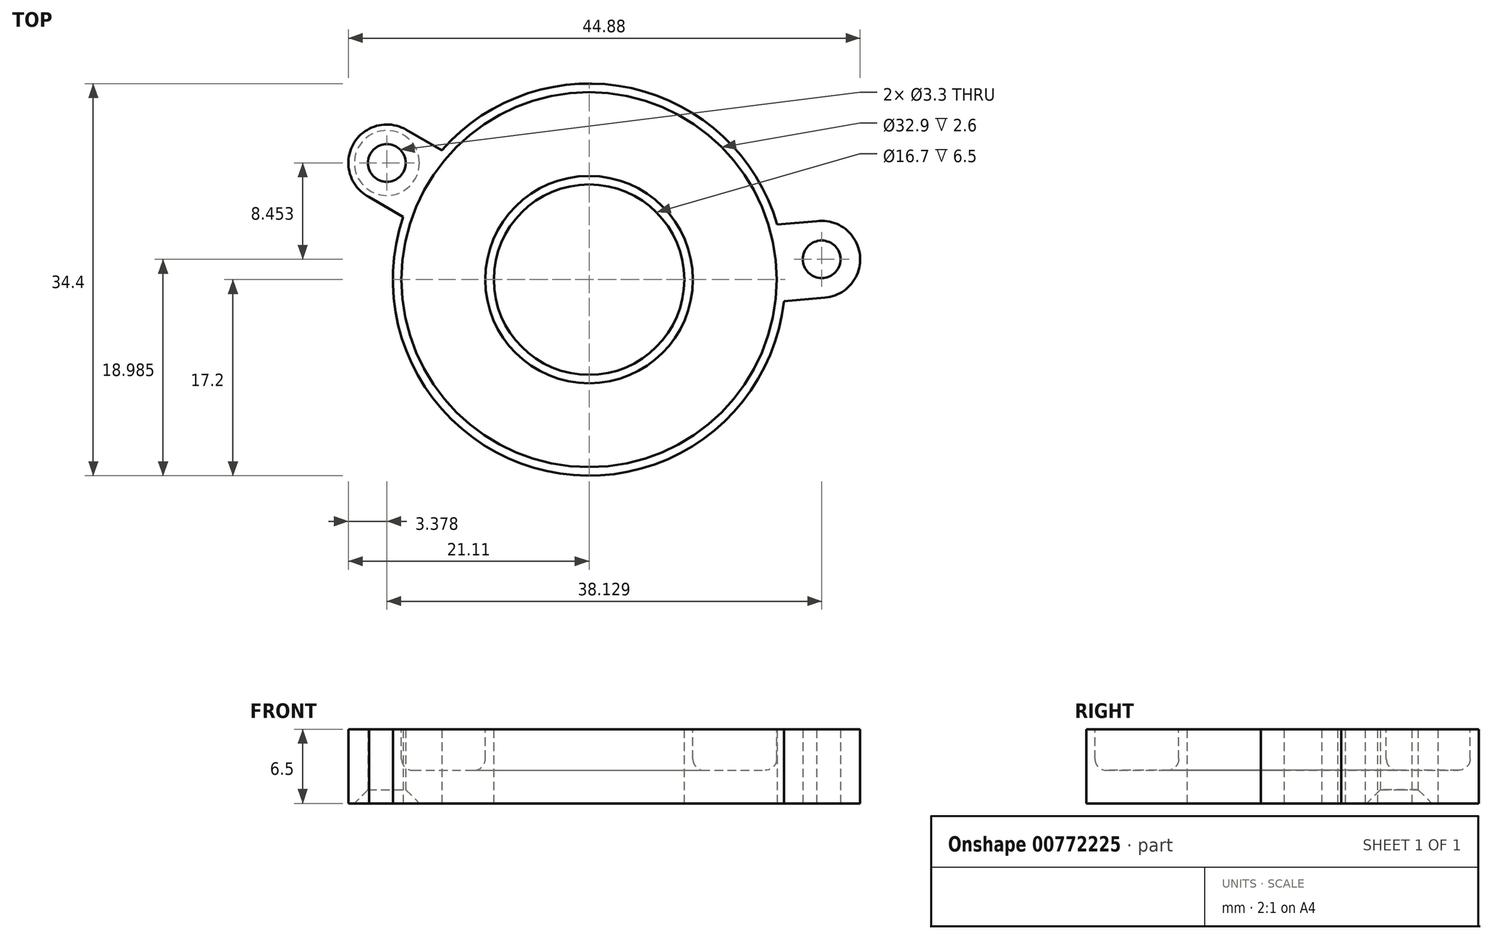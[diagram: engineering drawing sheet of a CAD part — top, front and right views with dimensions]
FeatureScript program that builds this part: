
annotation { "Feature Type Name" : "Feature", "Feature Type Description" : "" }
export const myFeature = defineFeature(function(context is Context, id is Id, definition is map)
    precondition{}
    {
        {
            var Q0;
            Q0=qCreatedBy(makeId("Right.planeOp"),FACE);
            var sketch = newSketch(context, id + "F0", { "sketchPlane" : qUnion([Q0])});
            skLineSegment(sketch, "E0.bottom", {"start": v(17.2, 0) * mm, "end": v(8.35, 0) * mm});
            skLineSegment(sketch, "E0.top", {"start": v(17.2, 6.5) * mm, "end": v(16.45, 6.5) * mm});
            skLineSegment(sketch, "E0.left", {"start": v(17.2, 6.5) * mm, "end": v(17.2, 0) * mm});
            skLineSegment(sketch, "E0.right", {"start": v(8.35, 6.5) * mm, "end": v(8.35, 0) * mm});
            skLineSegment(sketch, "E1.top", {"start": v(16.45, 2.9) * mm, "end": v(9.1, 2.9) * mm});
            skLineSegment(sketch, "E1.left", {"start": v(16.45, 2.9) * mm, "end": v(16.45, 6.5) * mm});
            skLineSegment(sketch, "E1.right", {"start": v(9.1, 2.9) * mm, "end": v(9.1, 6.5) * mm});
            skLineSegment(sketch, "E2.trimOffspring", {"start": v(9.1, 6.5) * mm, "end": v(8.35, 6.5) * mm});
            skLineSegment(sketch, "E3", {"start": v(0, 14.54) * mm, "end": v(0, -19.43) * mm, "construction": true});
            skSolve(sketch);
        }
        {
            var Q0;
            Q0=qSketchRegion(id+"F0",true);
            var Q1;
            Q1=sQuery(id+"F0.wireOp",EDGE,"E3");
            revolve(context, id + "F1", {"entities" : qUnion([Q0]), "axis" : qUnion([Q1]), "revolveType" : RevolveType.FULL});
        }
        {
            var Q0;
            Q0=qCreatedBy(makeId("Top.planeOp"),FACE);
            var sketch = newSketch(context, id + "F2", { "sketchPlane" : qUnion([Q0])});
            skArc(sketch, "E4", {"start": v(-16.04, 13.16) * mm, "mid": v(-20.69, 11.86) * mm, "end": v(-19.3, 7.25) * mm});
            skLineSegment(sketch, "E5", {"start": v(0, 0) * mm, "end": v(-17.73, 10.24) * mm, "construction": true});
            skLineSegment(sketch, "E6", {"start": v(-19.3, 7.25) * mm, "end": v(-16.3, 5.51) * mm});
            skLineSegment(sketch, "E7", {"start": v(-16.04, 13.16) * mm, "end": v(-12.92, 11.36) * mm});
            skArc(sketch, "E8.0", {"start": v(-12.92, 11.36) * mm, "mid": v(-14.9, 8.6) * mm, "end": v(-16.3, 5.51) * mm});
            skCircle(sketch, "E9", {"center": v(-17.73, 10.24) * mm, "radius": 1.65 * mm});
            skArc(sketch, "E10.1.0", {"start": v(17.1, -1.9) * mm, "mid": v(17.13, 1.5) * mm, "end": v(16.5, 4.83) * mm});
            skLineSegment(sketch, "E10.1.1", {"start": v(19.96, 5.13) * mm, "end": v(16.5, 4.83) * mm});
            skArc(sketch, "E10.1.2", {"start": v(20.7, -1.58) * mm, "mid": v(23.75, 2.15) * mm, "end": v(19.96, 5.13) * mm});
            skLineSegment(sketch, "E10.1.3", {"start": v(20.7, -1.58) * mm, "end": v(17.1, -1.9) * mm});
            skCircle(sketch, "E10.1.4", {"center": v(20.4, 1.78) * mm, "radius": 1.65 * mm});
            skLineSegment(sketch, "E10.1.5", {"start": v(0, 0) * mm, "end": v(20.4, 1.78) * mm, "construction": true});
            skLineSegment(sketch, "E10.anchor2", {"start": v(0, 0) * mm, "end": v(20.4, 1.78) * mm, "construction": true});
            skSolve(sketch);
        }
        {
            var Q0;
            Q0=qSketchRegion(id+"F2",true);
            var Q1;
            Q1=makeQuery(id+"F1.opRevolve","SWEPT_FACE",FACE,{"disambiguationData":[OSD([sQuery(id+"F0.wireOp",EDGE,"E0.top")])]});
            extrude(context, id + "F3", {"entities" : qUnion([Q0]), "operationType" : NewBodyOperationType.ADD, "endBound" : BoundingType.UP_TO_SURFACE, "endBoundEntityFace" : qUnion([Q1]), "depth" : 25 * mm});
        }
        {
            var Q0;
            Q0=makeQuery(id+"F3.opExtrude","CAP_EDGE",EDGE,{"disambiguationData":[OSD([sQuery(id+"F2.wireOp",EDGE,"cc04cc74-61d3-4c71-b712-62b44d6aaf24.1.2")])],"isStart":true});
            var Q1;
            Q1=makeQuery(id+"F3.opExtrude","CAP_EDGE",EDGE,{"disambiguationData":[OSD([sQuery(id+"F2.wireOp",EDGE,"E9")])],"isStart":true});
            chamfer(context, id + "F4", {"entities" : qUnion([Q0, Q1]), "width" : 1.2 * mm, "tangentPropagation" : true});
        }
        {
            var Q0;
            Q0=makeQuery(id+"F1.opRevolve","SWEPT_EDGE",EDGE,{"disambiguationData":[OSD([sQuery(id+"F0.wireOp",EDGE,"E1.top"),sQuery(id+"F0.wireOp",EDGE,"E1.left")])]});
            var Q1;
            Q1=makeQuery(id+"F1.opRevolve","SWEPT_EDGE",EDGE,{"disambiguationData":[OSD([sQuery(id+"F0.wireOp",EDGE,"E1.top"),sQuery(id+"F0.wireOp",EDGE,"E1.right")])]});
            fillet(context, id + "F5", {"entities" : qUnion([Q0, Q1]), "radius" : 1 * mm, "tangentPropagation" : true, "allowEdgeOverflow" : false});
        }
    });
